# Revit family: Data_Device-Work_Area-Leviton-QuickPort-Wallplate
name_source: partatom
category: Data Devices
units: mm (PartAtom-declared; Revit-internal decimal feet)

## family parameters
Classification Number = 23.85.50.21
Cut with Voids When Loaded = No
Host = Face
Maintain Annotation Orientation = Yes
Part Type = Normal
Room Calculation Point = No
Round Connector Dimension = Use Diameter
Shared = Yes

## types (1)
- ERROR *See Type Catalog*
    Annotation Symbol is Visible = Yes
    Assembly Code = D5030600
    Date Last Modified = October 30, 2023
    Default Elevation = 24 "
    Description = QuickPort Wallplate, Stainless Steel, 1 Port, Single Gang, Recessed
    Equipment Abbreviation = QPW
    Family Version = 1.0.9
    Has ID Windows = No
    Manufacturer = Leviton
    Minimum Order Quantity = 0
    Model Disclaimer = http://www.leviton.com
    Part Description = QuickPort Wallplate, Stainless Steel, 1 Port, Single Gang, Recessed
    Product Documentation Link = http://www.leviton.com
    Quantity per Package = 0
    Size Midway = No
    Size Standard = Yes
    Stainless Steel = Yes
    URL = http://www.leviton.com
    z 1 X Offset 1 = 1.231 "
    z 1 X Offset 2 = 3 "
    z 1 Y Offset 1 = 0.245 "
    z 2 Y Offset 2 = 0 "
    z Angles are Visible 2 Port = No
    z Angles are Visible 2 Port Plastic = No
    z Angles are Visible 4 Port = No
    z Angles are Visible 4 Port Dual Gang = No
    z Angles are Visible 4 Port Plastic = No
    z Collapse = Yes
    z Depth = 0.25 "
    z Distance = 0 "
    z Has 01 Port = Yes
    z Has 02 H Ports = No
    z Has 02 Ports = No
    z Has 03 Ports = No
    z Has 04 Ports = No
    z Has 06 Ports = No
    z Has 08 Ports = No
    z Has 12 Ports = No
    z Height = 0.65 "
    z Is Dual Gang = No
    z Is Single Gang = Yes
    z Leviton Type = 11
    z Offset 1 = 2 "
    z Offset 2 = 9 "
    z Offset 2 H = 9 "
    z Offset 3 = 9 "
    z Offset 4 = 9 "
    z Offset 6 = 9 "
    z Void 1 Port Angled = 6 "
    z Void 2 Port Angled = 8 "
    z Void 4 Port Angled = 8 "
    z Void Offset Angled = 0.735 "
    z Void Offset Angled Plastic = 0.0775 "
    z Void Offset Dual Gang 1 = 9 "
    z Void Offset Dual Gang 2 = 9 "
    z Void Offset Dual Gang 3 = 9 "
    z Void Offset Single Gang 1 = 9 "
    z Void Offset Single Gang 2 = 0.15 "
    z Void Offset Single Gang 3 = 9 "
    z Void Offset Single Gang 4 = 9 "
    z Width = 0.58 "

## geometry (parser evidence)
native form markers: Blend x32, Sweep x5
no freeform markers — native parametric forms only
